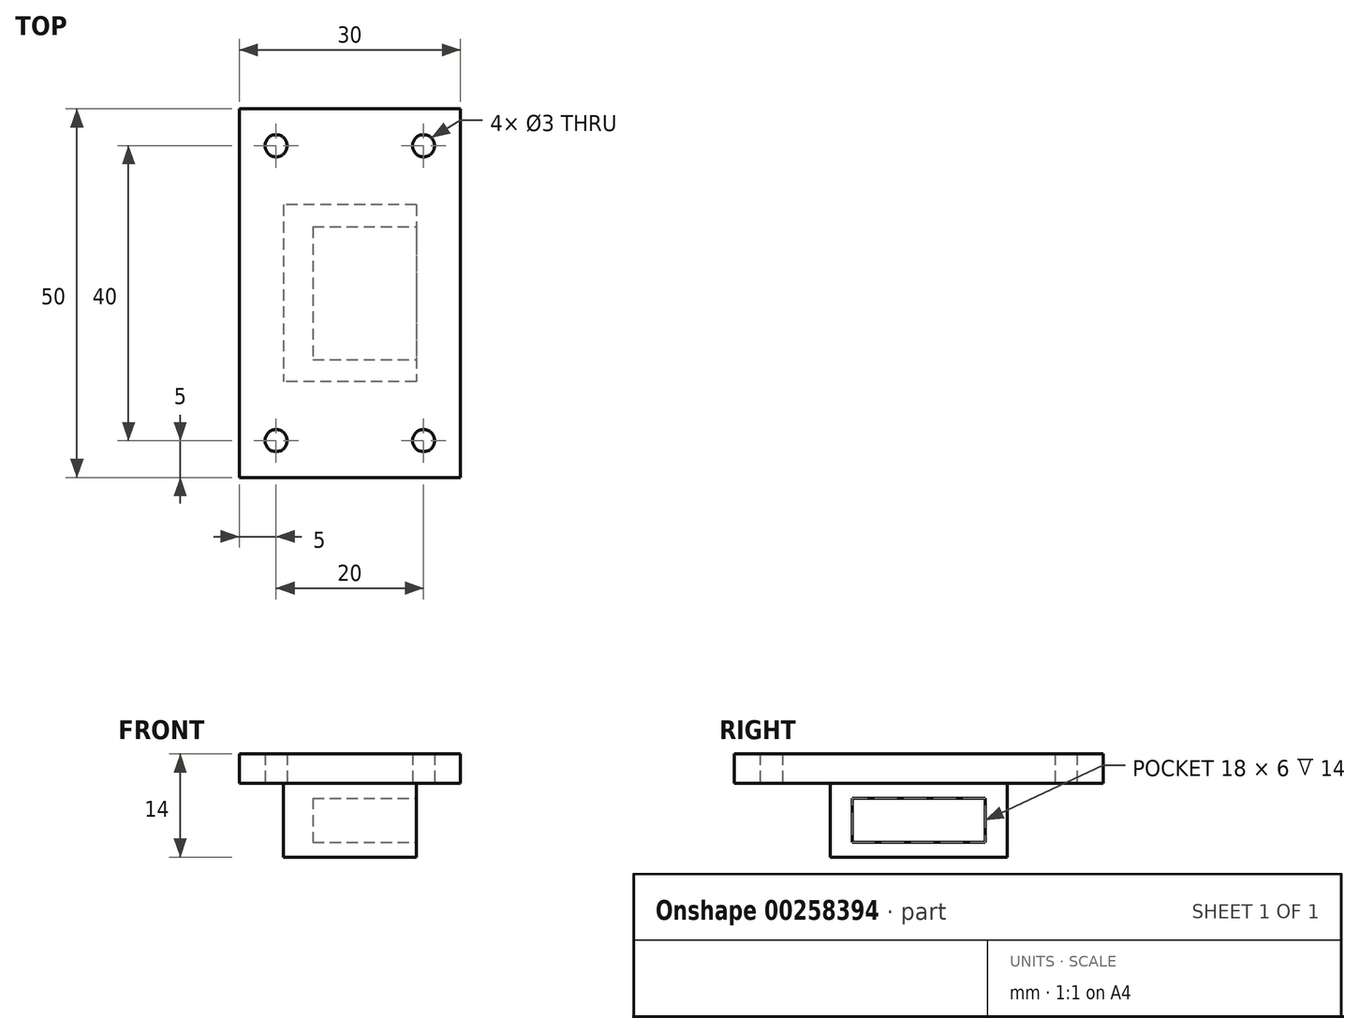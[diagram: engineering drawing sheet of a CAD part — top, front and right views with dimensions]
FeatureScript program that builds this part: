
annotation { "Feature Type Name" : "Feature", "Feature Type Description" : "" }
export const myFeature = defineFeature(function(context is Context, id is Id, definition is map)
    precondition{}
    {
        {
            var Q0;
            Q0=qCreatedBy(makeId("Top.planeOp"),FACE);
            var sketch = newSketch(context, id + "F0", { "sketchPlane" : qUnion([Q0])});
            skLineSegment(sketch, "E0.bottom", {"start": v(15, -25) * mm, "end": v(-15, -25) * mm});
            skLineSegment(sketch, "E0.top", {"start": v(15, 25) * mm, "end": v(-15, 25) * mm});
            skLineSegment(sketch, "E0.left", {"start": v(15, -25) * mm, "end": v(15, 25) * mm});
            skLineSegment(sketch, "E0.right", {"start": v(-15, -25) * mm, "end": v(-15, 25) * mm});
            skPoint(sketch, "E0.middle", {"position": v(0, 0) * mm});
            skCircle(sketch, "E1", {"center": v(-10, 20) * mm, "radius": 1.5 * mm});
            skCircle(sketch, "E2.MirrorC", {"center": v(10, 20) * mm, "radius": 1.5 * mm});
            skCircle(sketch, "E3.MirrorC", {"center": v(-10, -20) * mm, "radius": 1.5 * mm});
            skCircle(sketch, "E4.MirrorC", {"center": v(10, -20) * mm, "radius": 1.5 * mm});
            skSolve(sketch);
        }
        {
            var Q0;
            Q0=makeQuery(id+"F0.imprint","IMPRINT",FACE,{"disambiguationData":[TD([[makeQuery(id+"F0.imprint","IMPRINT",EDGE,{"derivedFrom":sQuery(id+"F0.wireOp",EDGE,"E0.bottom")}),-1.0]])]});
            extrude(context, id + "F1", {"entities" : qUnion([Q0]), "depth" : 4 * mm});
        }
        {
            var Q0;
            Q0=makeQuery(id+"F1.opExtrude","CAP_FACE",FACE,{"disambiguationData":[OSD([sQuery(id+"F0.wireOp",EDGE,"E0.bottom"),sQuery(id+"F0.wireOp",EDGE,"E0.top"),sQuery(id+"F0.wireOp",EDGE,"E0.left"),sQuery(id+"F0.wireOp",EDGE,"E0.right"),sQuery(id+"F0.wireOp",EDGE,"E1"),sQuery(id+"F0.wireOp",EDGE,"E2.MirrorC"),sQuery(id+"F0.wireOp",EDGE,"E3.MirrorC"),sQuery(id+"F0.wireOp",EDGE,"E4.MirrorC")])],"isStart":true});
            var sketch = newSketch(context, id + "F2", { "sketchPlane" : qUnion([Q0])});
            skLineSegment(sketch, "E5.bottom", {"start": v(9, -12) * mm, "end": v(-9, -12) * mm});
            skLineSegment(sketch, "E5.top", {"start": v(9, 12) * mm, "end": v(-9, 12) * mm});
            skLineSegment(sketch, "E5.left", {"start": v(9, -12) * mm, "end": v(9, 12) * mm});
            skLineSegment(sketch, "E5.right", {"start": v(-9, -12) * mm, "end": v(-9, 12) * mm});
            skPoint(sketch, "E5.middle", {"position": v(0, 0) * mm});
            skSolve(sketch);
        }
        {
            var Q0;
            Q0=makeQuery(id+"F2.imprint","IMPRINT",FACE,{"disambiguationData":[TD([[makeQuery(id+"F2.imprint","IMPRINT",EDGE,{"derivedFrom":sQuery(id+"F2.wireOp",EDGE,"E5.bottom")}),-1.0]])]});
            extrude(context, id + "F3", {"entities" : qUnion([Q0]), "operationType" : NewBodyOperationType.ADD, "depth" : 10 * mm});
        }
        {
            var Q0;
            Q0=makeQuery(id+"F3.opExtrude","SWEPT_FACE",FACE,{"disambiguationData":[OSD([sQuery(id+"F2.wireOp",EDGE,"E5.left")])]});
            var sketch = newSketch(context, id + "F4", { "sketchPlane" : qUnion([Q0])});
            skLineSegment(sketch, "E6.bottom", {"start": v(9, -2) * mm, "end": v(-9, -2) * mm});
            skLineSegment(sketch, "E6.top", {"start": v(9, -8) * mm, "end": v(-9, -8) * mm});
            skLineSegment(sketch, "E6.left", {"start": v(9, -2) * mm, "end": v(9, -8) * mm});
            skLineSegment(sketch, "E6.right", {"start": v(-9, -2) * mm, "end": v(-9, -8) * mm});
            skPoint(sketch, "E6.middle", {"position": v(0, -5) * mm});
            skPoint(sketch, "E6.middle.positionSnap0", {"position": v(-12, -5) * mm});
            skPoint(sketch, "E6.middle.positionSnap1", {"position": v(0, -10) * mm});
            skPoint(sketch, "E6.centerSnap0", {"position": v(-12, -5) * mm});
            skPoint(sketch, "E6.centerSnap1", {"position": v(0, -10) * mm});
            skSolve(sketch);
        }
        {
            var Q0;
            Q0=makeQuery(id+"F4.imprint","IMPRINT",FACE,{"disambiguationData":[TD([[makeQuery(id+"F4.imprint","IMPRINT",EDGE,{"derivedFrom":sQuery(id+"F4.wireOp",EDGE,"E6.bottom")}),1.0]])]});
            extrude(context, id + "F5", {"entities" : qUnion([Q0]), "operationType" : NewBodyOperationType.REMOVE, "oppositeDirection" : true, "depth" : 14 * mm});
        }
    });
